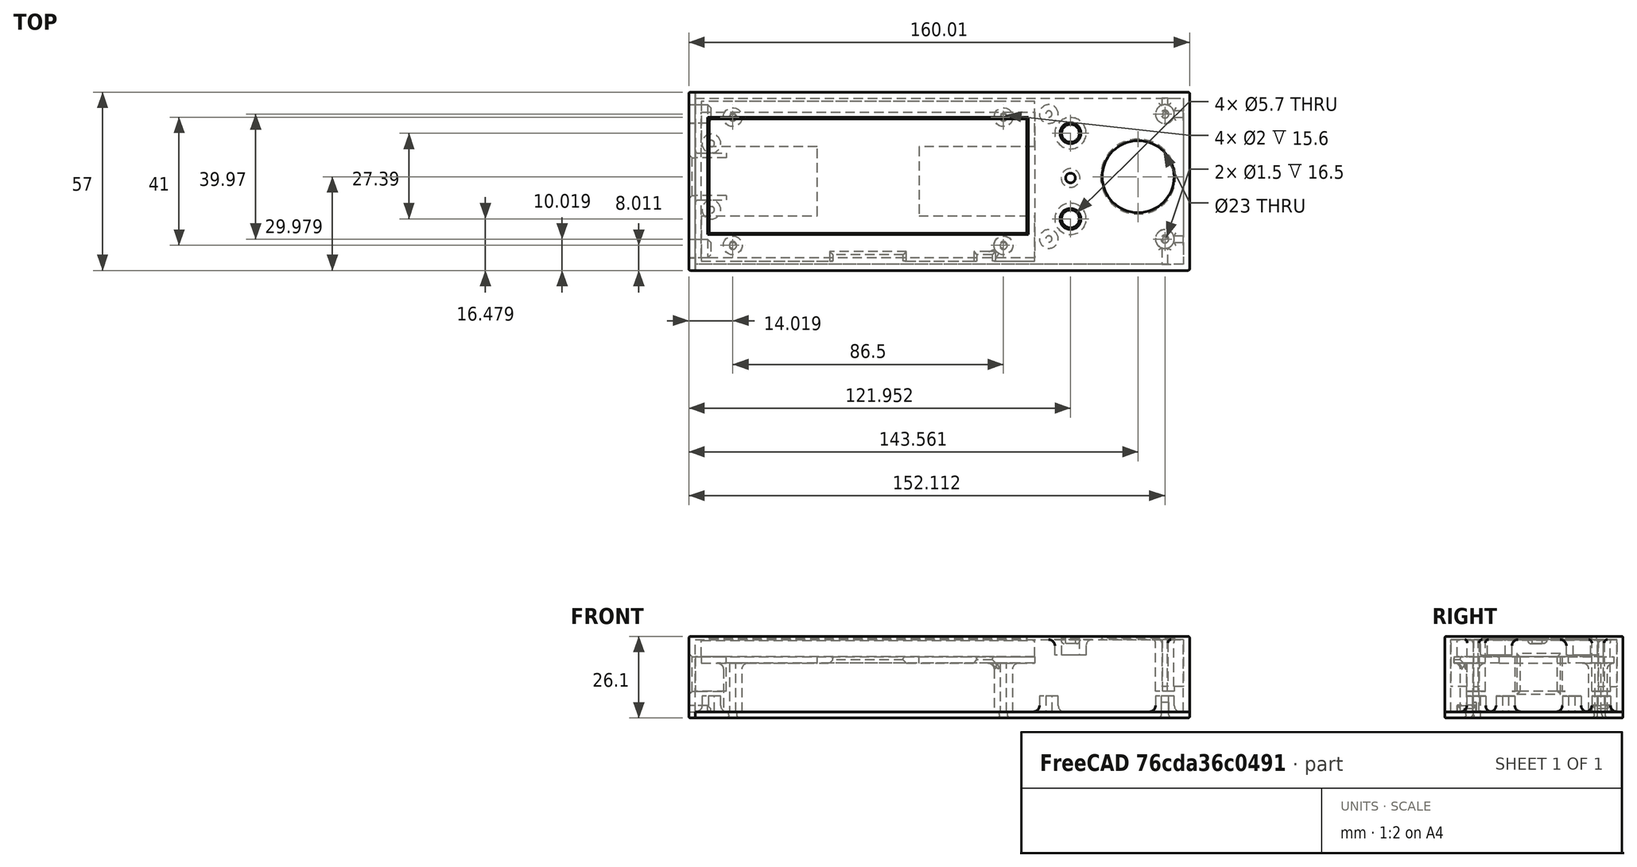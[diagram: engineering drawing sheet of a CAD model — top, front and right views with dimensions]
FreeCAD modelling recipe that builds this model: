
FCSTD DOCUMENT  (FreeCAD 0.15R4671 (Git))
Label: together
License: All rights reserved
LicenseURL: http://en.wikipedia.org/wiki/All_rights_reserved
objects: Part::Feature×3, App::VRMLObject×1, Sketcher::SketchObject×1, PartDesign::Pad×1
note: 6 computed .brp shape members not serialized (recipe doc carries the construction recipe); baked Part::Feature solids carry a one-line shape summary decoded from their .brp

FEATURE [Part::Feature] Fillet009_solid  label="bottom"
  shape: bbox 160 x 57 x 7 mm, 74 faces (baked)
FEATURE [Part::Feature] Fillet002_solid  label="table"
  Placement = pos=(7.665,-2.95,19.6) rot=(0,1,0;3.14159rad)
  shape: bbox 106.5 x 51.82 x 17.6 mm, 57 faces (baked)
FEATURE [App::VRMLObject] rozhrani_semestralka  label="dps"
  Placement = pos=(-152.3,92.75,7.5) rot=(0,0,1;0rad)
FEATURE [Sketcher::SketchObject] Sketch
  Placement = pos=(-13.05,-10.5,19.6) rot=(0,0,1;0rad)
  sketch-geometry (4):
    g0: LineSegment StartX=-64.5702 StartY=17.7261 StartZ=0 EndX=41.9198 EndY=17.7261 EndZ=0
    g1: LineSegment StartX=41.9198 StartY=17.7261 StartZ=0 EndX=41.9198 EndY=-28.9339 EndZ=0
    g2: LineSegment StartX=41.9198 StartY=-28.9339 StartZ=0 EndX=-64.5702 EndY=-28.9339 EndZ=0
    g3: LineSegment StartX=-64.5702 StartY=-28.9339 StartZ=0 EndX=-64.5702 EndY=17.7261 EndZ=0
  constraints (10):
    c: Coincident(g0,g1)
    c: Coincident(g1,g2)
    c: Coincident(g2,g3)
    c: Coincident(g3,g0)
    c: Horizontal(g0)
    c: Horizontal(g2)
    c: Vertical(g1)
    c: Vertical(g3)
    c: Distance(g0) = 106.49
    c: Distance(g3) = 46.66
FEATURE [PartDesign::Pad] Pad  label="lcd"
  Length = 5.2
  Length2 = 100
  Placement = pos=(-13.05,-10.5,19.6) rot=(0,0,1;0rad)
  Sketch = -> Sketch
  Type = 0
FEATURE [Part::Feature] Fillet013_solid  label="top"
  Placement = pos=(-9.9,-6.75,2) rot=(0,0,1;0rad)
  shape: bbox 160 x 57 x 26.1 mm, 132 faces (baked)
